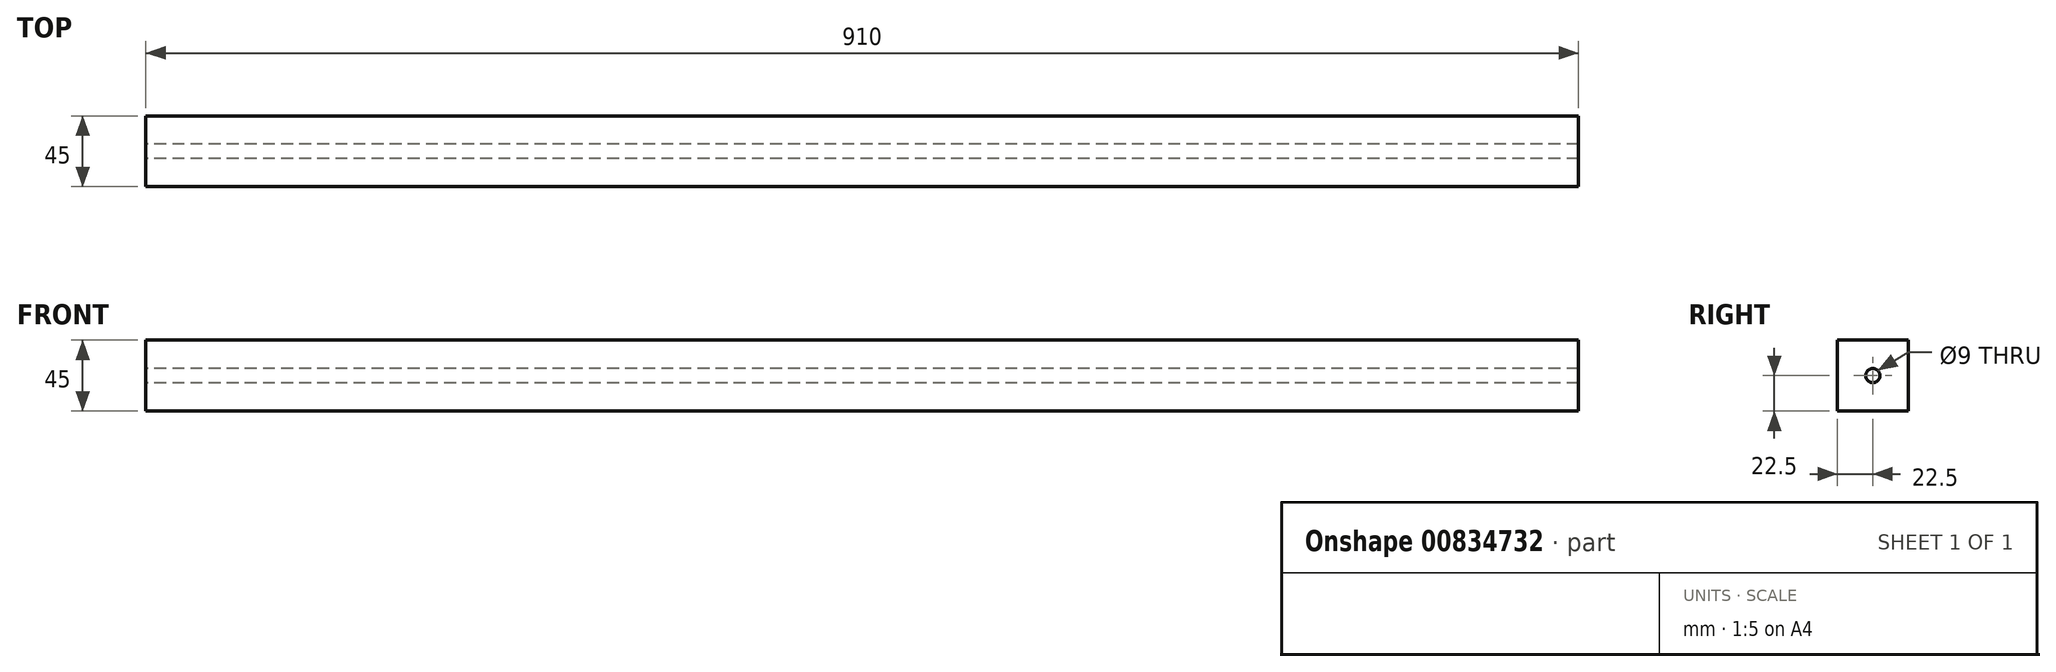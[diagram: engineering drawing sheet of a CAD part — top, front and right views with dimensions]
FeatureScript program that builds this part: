
annotation { "Feature Type Name" : "Feature", "Feature Type Description" : "" }
export const myFeature = defineFeature(function(context is Context, id is Id, definition is map)
    precondition{}
    {
        {
            var Q0;
            Q0=qCreatedBy(makeId("Right.planeOp"),FACE);
            var sketch = newSketch(context, id + "F0", { "sketchPlane" : qUnion([Q0])});
            skLineSegment(sketch, "E0.bottom", {"start": v(22.5, -22.5) * mm, "end": v(-22.5, -22.5) * mm});
            skLineSegment(sketch, "E0.top", {"start": v(22.5, 22.5) * mm, "end": v(-22.5, 22.5) * mm});
            skLineSegment(sketch, "E0.left", {"start": v(22.5, -22.5) * mm, "end": v(22.5, 22.5) * mm});
            skLineSegment(sketch, "E0.right", {"start": v(-22.5, -22.5) * mm, "end": v(-22.5, 22.5) * mm});
            skPoint(sketch, "E0.middle", {"position": v(0, 0) * mm});
            skCircle(sketch, "E1", {"center": v(0, 0) * mm, "radius": 4.5 * mm});
            skSolve(sketch);
        }
        {
            var Q0;
            Q0 = qSketchRegion(id + "F0", true);
            extrude(context, id + "F1", {"entities" : qUnion([Q0]), "depth" : 910 * mm, "offsetDistance" : 25 * mm});
        }
    });
